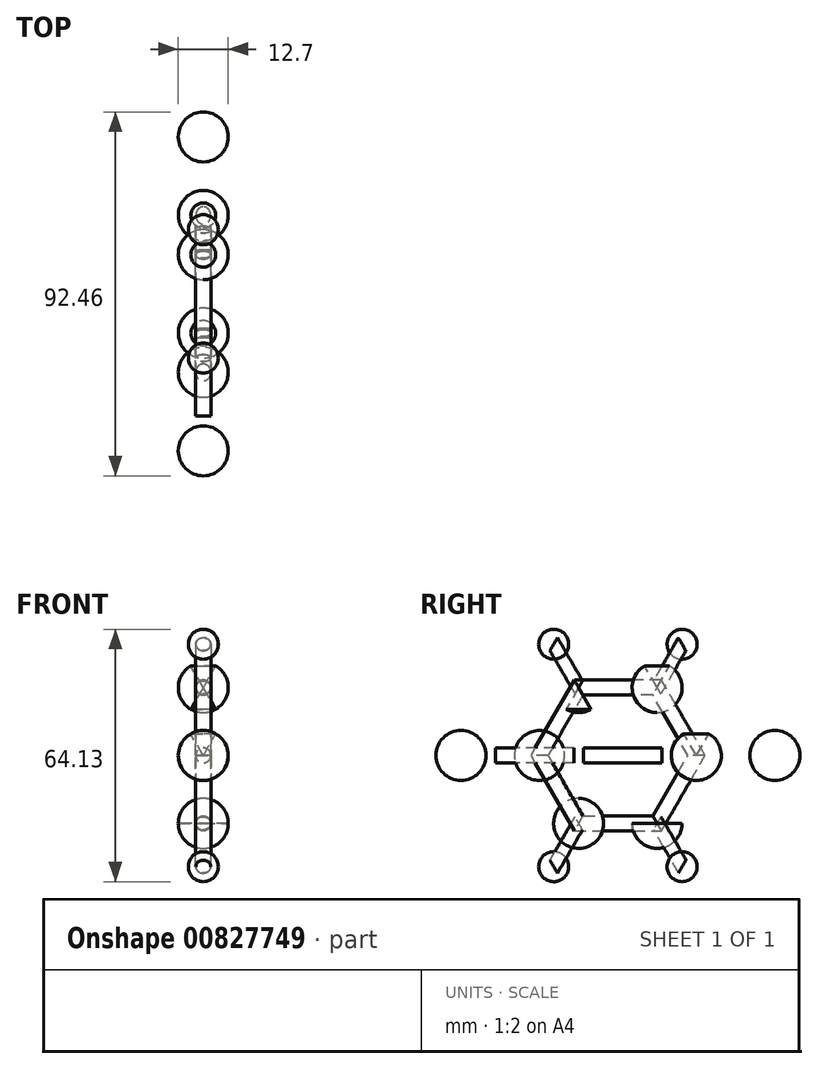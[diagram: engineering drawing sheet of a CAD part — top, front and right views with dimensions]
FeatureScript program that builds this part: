
annotation { "Feature Type Name" : "Feature", "Feature Type Description" : "" }
export const myFeature = defineFeature(function(context is Context, id is Id, definition is map)
    precondition{}
    {
        {
            var Q0;
            Q0=qCreatedBy(makeId("Front.planeOp"),FACE);
            var sketch = newSketch(context, id + "F0", { "sketchPlane" : qUnion([Q0])});
            skArc(sketch, "E0", {"start": v(0, 6.35) * mm, "mid": v(-6.35, 0) * mm, "end": v(0, -6.35) * mm});
            skLineSegment(sketch, "E1", {"start": v(0, 6.35) * mm, "end": v(0, -6.35) * mm});
            skSolve(sketch);
        }
        {
            var Q0;
            Q0=makeQuery(id+"F0.imprint","IMPRINT",FACE,{"disambiguationData":[TD([[makeQuery(id+"F0.imprint","IMPRINT",EDGE,{"derivedFrom":sQuery(id+"F0.wireOp",EDGE,"E0")}),1.0]])]});
            var Q1;
            Q1=sQuery(id+"F0.wireOp",EDGE,"E1");
            revolve(context, id + "F1", {"surfaceOperationType" : NewSurfaceOperationType.NEW, "entities" : qUnion([Q0]), "axis" : qUnion([Q1]), "revolveType" : RevolveType.FULL});
        }
        {
            var Q0;
            Q0=qCreatedBy(makeId("Right.planeOp"),FACE);
            var sketch = newSketch(context, id + "F2", { "sketchPlane" : qUnion([Q0])});
            skLineSegment(sketch, "E2", {"start": v(0, 0) * mm, "end": v(19.93, 0) * mm});
            skLineSegment(sketch, "E3", {"start": v(19.93, 0) * mm, "end": v(29.9, 17.26) * mm});
            skLineSegment(sketch, "E4", {"start": v(29.9, 17.26) * mm, "end": v(19.93, 34.52) * mm});
            skLineSegment(sketch, "E5", {"start": v(19.93, 34.52) * mm, "end": v(0, 34.52) * mm});
            skLineSegment(sketch, "E6", {"start": v(0, 34.52) * mm, "end": v(-9.96, 17.26) * mm});
            skLineSegment(sketch, "E7", {"start": v(-9.96, 17.26) * mm, "end": v(0, 0) * mm});
            skArc(sketch, "E8", {"start": v(19.93, 6.35) * mm, "mid": v(13.58, 0) * mm, "end": v(19.93, -6.35) * mm});
            skArc(sketch, "E9", {"start": v(29.9, 23.6) * mm, "mid": v(23.54, 17.26) * mm, "end": v(29.9, 10.9) * mm});
            skArc(sketch, "E10", {"start": v(19.93, 28.17) * mm, "mid": v(26.28, 34.52) * mm, "end": v(19.93, 40.87) * mm});
            skArc(sketch, "E11", {"start": v(-9.96, 23.6) * mm, "mid": v(-16.31, 17.26) * mm, "end": v(-9.96, 10.9) * mm});
            skLineSegment(sketch, "E12", {"start": v(19.93, 0) * mm, "end": v(19.93, 6.35) * mm});
            skLineSegment(sketch, "E13", {"start": v(19.93, 6.35) * mm, "end": v(19.93, -6.35) * mm});
            skLineSegment(sketch, "E14", {"start": v(29.9, 17.26) * mm, "end": v(29.9, 23.6) * mm});
            skLineSegment(sketch, "E15", {"start": v(29.9, 23.6) * mm, "end": v(29.9, 10.9) * mm});
            skLineSegment(sketch, "E16", {"start": v(19.93, 34.52) * mm, "end": v(19.93, 40.87) * mm});
            skLineSegment(sketch, "E17", {"start": v(19.93, 40.87) * mm, "end": v(19.93, 28.17) * mm});
            skLineSegment(sketch, "E18", {"start": v(0, 34.52) * mm, "end": v(0, 40.87) * mm});
            skLineSegment(sketch, "E19", {"start": v(0, 40.87) * mm, "end": v(0, 28.17) * mm});
            skLineSegment(sketch, "E20", {"start": v(-9.96, 17.26) * mm, "end": v(-9.96, 23.6) * mm});
            skLineSegment(sketch, "E21", {"start": v(-9.96, 23.6) * mm, "end": v(-9.96, 10.9) * mm});
            skArc(sketch, "E22.trimOffspring", {"start": v(0, 40.87) * mm, "mid": v(-6.13, 36.16) * mm, "end": v(-3.18, 29.02) * mm});
            skArc(sketch, "E23", {"start": v(0, 40.87) * mm, "mid": v(-6.35, 34.52) * mm, "end": v(0, 28.17) * mm});
            skLineSegment(sketch, "E24", {"start": v(19.93, 34.52) * mm, "end": v(26.28, 45.51) * mm});
            skLineSegment(sketch, "E25", {"start": v(0, 34.52) * mm, "end": v(-6.35, 45.51) * mm});
            skLineSegment(sketch, "E26", {"start": v(19.93, 0) * mm, "end": v(26.28, -11) * mm});
            skLineSegment(sketch, "E27", {"start": v(0, 0) * mm, "end": v(-6.35, -11) * mm});
            skArc(sketch, "E28", {"start": v(26.28, 41.7) * mm, "mid": v(30.09, 45.51) * mm, "end": v(26.28, 49.32) * mm});
            skArc(sketch, "E29", {"start": v(-6.35, 49.32) * mm, "mid": v(-10.16, 45.51) * mm, "end": v(-6.35, 41.7) * mm});
            skArc(sketch, "E30", {"start": v(26.28, -7.19) * mm, "mid": v(22.47, -11) * mm, "end": v(26.28, -14.8) * mm});
            skArc(sketch, "E31", {"start": v(-6.35, -14.8) * mm, "mid": v(-2.54, -11) * mm, "end": v(-6.35, -7.19) * mm});
            skLineSegment(sketch, "E32", {"start": v(26.28, 45.51) * mm, "end": v(26.28, 49.32) * mm});
            skLineSegment(sketch, "E33", {"start": v(26.28, 49.32) * mm, "end": v(26.28, 41.7) * mm});
            skLineSegment(sketch, "E34", {"start": v(-6.35, 45.51) * mm, "end": v(-6.35, 49.32) * mm});
            skLineSegment(sketch, "E35", {"start": v(-6.35, 49.32) * mm, "end": v(-6.35, 41.7) * mm});
            skLineSegment(sketch, "E36", {"start": v(-6.35, -11) * mm, "end": v(-6.35, -7.19) * mm});
            skLineSegment(sketch, "E37", {"start": v(-6.35, -7.19) * mm, "end": v(-6.35, -14.8) * mm});
            skLineSegment(sketch, "E38", {"start": v(26.28, -11) * mm, "end": v(26.28, -7.19) * mm});
            skLineSegment(sketch, "E39", {"start": v(26.28, -7.19) * mm, "end": v(26.28, -14.8) * mm});
            skSolve(sketch);
        }
        {
            var Q0;
            {var subQ0=sQuery(id+"F2.wireOp",EDGE,"E19");var subQ3=sQuery(id+"F2.wireOp",EDGE,"E23");var subQ5=makeQuery(id+"F2.imprint","INTERSECT",VERTEX,{"disambiguationData":[OD(0.0)],"derivedFrom":[subQ0,subQ3]});Q0=makeQuery(id+"F2.imprint","IMPRINT",FACE,{"disambiguationData":[TD([[makeQuery(id+"F2.imprint","IMPRINT",EDGE,{"disambiguationData":[TD([[subQ5,-1.0]])],"derivedFrom":subQ3}),1.0]])]});}
            var Q1;
            {var subQ0=sQuery(id+"F2.wireOp",EDGE,"E19");var subQ3=sQuery(id+"F2.wireOp",EDGE,"E23");var subQ5=makeQuery(id+"F2.imprint","INTERSECT",VERTEX,{"disambiguationData":[OD(1.0)],"derivedFrom":[subQ0,subQ3]});Q1=makeQuery(id+"F2.imprint","IMPRINT",FACE,{"disambiguationData":[TD([[makeQuery(id+"F2.imprint","IMPRINT",EDGE,{"disambiguationData":[TD([[subQ5,1.0]])],"derivedFrom":subQ3}),1.0]])]});}
            var Q2;
            {var subQ0=sQuery(id+"F2.wireOp",EDGE,"E25");var subQ3=sQuery(id+"F2.wireOp",EDGE,"E23");var subQ5=makeQuery(id+"F2.imprint","INTERSECT",VERTEX,{"derivedFrom":[subQ3,subQ0]});Q2=makeQuery(id+"F2.imprint","IMPRINT",FACE,{"disambiguationData":[TD([[makeQuery(id+"F2.imprint","IMPRINT",EDGE,{"disambiguationData":[TD([[subQ5,-1.0]])],"derivedFrom":subQ3}),1.0]])]});}
            var Q3;
            Q3=sQuery(id+"F2.wireOp",EDGE,"E18");
            revolve(context, id + "F3", {"surfaceOperationType" : NewSurfaceOperationType.NEW, "entities" : qUnion([Q0, Q1, Q2]), "axis" : qUnion([Q3]), "revolveType" : RevolveType.FULL});
        }
        {
            var Q0;
            {var subQ0=sQuery(id+"F2.wireOp",EDGE,"E11");Q0=makeQuery(id+"F2.imprint","IMPRINT",FACE,{"disambiguationData":[TD([[makeQuery(id+"F2.imprint","IMPRINT",EDGE,{"derivedFrom":subQ0}),1.0]])]});}
            var Q1;
            Q1=sQuery(id+"F2.wireOp",EDGE,"E20");
            revolve(context, id + "F4", {"surfaceOperationType" : NewSurfaceOperationType.NEW, "entities" : qUnion([Q0]), "axis" : qUnion([Q1]), "revolveType" : RevolveType.FULL});
        }
        {
            var Q0;
            {var subQ0=sQuery(id+"F2.wireOp",EDGE,"E24");var subQ3=sQuery(id+"F2.wireOp",EDGE,"E10");var subQ5=makeQuery(id+"F2.imprint","INTERSECT",VERTEX,{"derivedFrom":[subQ3,subQ0]});Q0=makeQuery(id+"F2.imprint","IMPRINT",FACE,{"disambiguationData":[TD([[makeQuery(id+"F2.imprint","IMPRINT",EDGE,{"disambiguationData":[TD([[subQ5,1.0]])],"derivedFrom":subQ3}),1.0]])]});}
            var Q1;
            {var subQ0=sQuery(id+"F2.wireOp",EDGE,"E17");var subQ3=sQuery(id+"F2.wireOp",EDGE,"E10");var subQ5=makeQuery(id+"F2.imprint","INTERSECT",VERTEX,{"disambiguationData":[OD(0.0)],"derivedFrom":[subQ3,subQ0]});Q1=makeQuery(id+"F2.imprint","IMPRINT",FACE,{"disambiguationData":[TD([[makeQuery(id+"F2.imprint","IMPRINT",EDGE,{"disambiguationData":[TD([[subQ5,-1.0]])],"derivedFrom":subQ3}),1.0]])]});}
            var Q2;
            {var subQ0=sQuery(id+"F2.wireOp",EDGE,"E17");var subQ1=sQuery(id+"F2.wireOp",EDGE,"E10");var subQ2=makeQuery(id+"F2.imprint","INTERSECT",VERTEX,{"disambiguationData":[OD(1.0)],"derivedFrom":[subQ1,subQ0]});Q2=makeQuery(id+"F2.imprint","IMPRINT",FACE,{"disambiguationData":[TD([[makeQuery(id+"F2.imprint","IMPRINT",EDGE,{"disambiguationData":[TD([[subQ2,1.0]])],"derivedFrom":subQ1}),1.0]])]});}
            var Q3;
            Q3=sQuery(id+"F2.wireOp",EDGE,"E17");
            revolve(context, id + "F5", {"surfaceOperationType" : NewSurfaceOperationType.NEW, "entities" : qUnion([Q0, Q1, Q2]), "axis" : qUnion([Q3]), "revolveType" : RevolveType.FULL});
        }
        {
            var Q0;
            {var subQ0=sQuery(id+"F2.wireOp",EDGE,"E15");var subQ3=sQuery(id+"F2.wireOp",EDGE,"E9");var subQ5=makeQuery(id+"F2.imprint","INTERSECT",VERTEX,{"disambiguationData":[OD(0.0)],"derivedFrom":[subQ3,subQ0]});Q0=makeQuery(id+"F2.imprint","IMPRINT",FACE,{"disambiguationData":[TD([[makeQuery(id+"F2.imprint","IMPRINT",EDGE,{"disambiguationData":[TD([[subQ5,-1.0]])],"derivedFrom":subQ3}),1.0]])]});}
            var Q1;
            {var subQ0=sQuery(id+"F2.wireOp",EDGE,"E15");var subQ3=sQuery(id+"F2.wireOp",EDGE,"E9");var subQ5=makeQuery(id+"F2.imprint","INTERSECT",VERTEX,{"disambiguationData":[OD(1.0)],"derivedFrom":[subQ3,subQ0]});Q1=makeQuery(id+"F2.imprint","IMPRINT",FACE,{"disambiguationData":[TD([[makeQuery(id+"F2.imprint","IMPRINT",EDGE,{"disambiguationData":[TD([[subQ5,1.0]])],"derivedFrom":subQ3}),1.0]])]});}
            var Q2;
            {var subQ1=sQuery(id+"F2.wireOp",EDGE,"E3");var subQ3=sQuery(id+"F2.wireOp",EDGE,"E9");var subQ4=makeQuery(id+"F2.imprint","INTERSECT",VERTEX,{"derivedFrom":[subQ1,subQ3]});Q2=makeQuery(id+"F2.imprint","IMPRINT",FACE,{"disambiguationData":[TD([[makeQuery(id+"F2.imprint","IMPRINT",EDGE,{"disambiguationData":[TD([[subQ4,1.0]])],"derivedFrom":subQ3}),1.0]])]});}
            var Q3;
            Q3=sQuery(id+"F2.wireOp",EDGE,"E14");
            revolve(context, id + "F6", {"surfaceOperationType" : NewSurfaceOperationType.NEW, "entities" : qUnion([Q0, Q1, Q2]), "axis" : qUnion([Q3]), "revolveType" : RevolveType.FULL});
        }
        {
            var Q0;
            {var subQ0=sQuery(id+"F2.wireOp",EDGE,"E13");var subQ3=sQuery(id+"F2.wireOp",EDGE,"E8");var subQ5=makeQuery(id+"F2.imprint","INTERSECT",VERTEX,{"disambiguationData":[OD(0.0)],"derivedFrom":[subQ3,subQ0]});Q0=makeQuery(id+"F2.imprint","IMPRINT",FACE,{"disambiguationData":[TD([[makeQuery(id+"F2.imprint","IMPRINT",EDGE,{"disambiguationData":[TD([[subQ5,-1.0]])],"derivedFrom":subQ3}),1.0]])]});}
            var Q1;
            {var subQ0=sQuery(id+"F2.wireOp",EDGE,"E13");var subQ3=sQuery(id+"F2.wireOp",EDGE,"E8");var subQ5=makeQuery(id+"F2.imprint","INTERSECT",VERTEX,{"disambiguationData":[OD(1.0)],"derivedFrom":[subQ3,subQ0]});Q1=makeQuery(id+"F2.imprint","IMPRINT",FACE,{"disambiguationData":[TD([[makeQuery(id+"F2.imprint","IMPRINT",EDGE,{"disambiguationData":[TD([[subQ5,1.0]])],"derivedFrom":subQ3}),1.0]])]});}
            var Q2;
            Q2=sQuery(id+"F2.wireOp",EDGE,"E13");
            revolve(context, id + "F7", {"surfaceOperationType" : NewSurfaceOperationType.NEW, "entities" : qUnion([Q0, Q1]), "axis" : qUnion([Q2]), "revolveType" : RevolveType.FULL});
        }
        {
            var Q0;
            Q0=qCreatedBy(makeId("Front.planeOp"),FACE);
            var sketch = newSketch(context, id + "F8", { "sketchPlane" : qUnion([Q0])});
            skCircle(sketch, "E40", {"center": v(0, 0) * mm, "radius": 1.9 * mm});
            skSolve(sketch);
        }
        {
            var Q0;
            Q0=makeQuery(id+"F8.imprint","IMPRINT",FACE,{"disambiguationData":[TD([[makeQuery(id+"F8.imprint","IMPRINT",EDGE,{"derivedFrom":sQuery(id+"F8.wireOp",EDGE,"E40")}),1.0]])]});
            var Q1;
            Q1=sQuery(id+"F2.wireOp",EDGE,"E2");
            var Q2;
            Q2=sQuery(id+"F2.wireOp",EDGE,"E3");
            var Q3;
            Q3=sQuery(id+"F2.wireOp",EDGE,"E4");
            var Q4;
            Q4=sQuery(id+"F2.wireOp",EDGE,"E5");
            var Q5;
            Q5=sQuery(id+"F2.wireOp",EDGE,"E6");
            var Q6;
            Q6=sQuery(id+"F2.wireOp",EDGE,"E7");
            var Q7;
            Q7 = qConstructionFilter(qBodyType(qCreatedBy(id + "F10" ,EDGE), BodyType.WIRE), ConstructionObject.NO);
            sweep(context, id + "F9", {"profiles" : qUnion([Q0]), "path" : qUnion([Q1, Q2, Q3, Q4, Q5, Q6, Q7])});
        }
        {
            var Q0;
            Q0=qCreatedBy(makeId("Right.planeOp"),FACE);
            var sketch = newSketch(context, id + "F10", { "sketchPlane" : qUnion([Q0])});
            skLineSegment(sketch, "E41", {"start": v(0, 0) * mm, "end": v(-9.97, 17.27) * mm});
            skLineSegment(sketch, "E42", {"start": v(-9.97, 17.27) * mm, "end": v(-29.9, 17.27) * mm});
            skLineSegment(sketch, "E43", {"start": v(0, 0) * mm, "end": v(19.94, 0) * mm});
            skLineSegment(sketch, "E44", {"start": v(19.94, 0) * mm, "end": v(29.9, 17.27) * mm});
            skLineSegment(sketch, "E45", {"start": v(29.9, 17.27) * mm, "end": v(49.85, 17.27) * mm});
            skArc(sketch, "E46", {"start": v(49.85, 10.92) * mm, "mid": v(56.2, 17.27) * mm, "end": v(49.85, 23.62) * mm});
            skArc(sketch, "E47", {"start": v(-29.9, 23.62) * mm, "mid": v(-36.26, 17.27) * mm, "end": v(-29.9, 10.92) * mm});
            skLineSegment(sketch, "E48", {"start": v(-29.9, 17.27) * mm, "end": v(-29.9, 23.62) * mm});
            skLineSegment(sketch, "E49", {"start": v(-29.9, 23.62) * mm, "end": v(-29.9, 10.92) * mm});
            skLineSegment(sketch, "E50", {"start": v(49.85, 17.27) * mm, "end": v(49.85, 23.62) * mm});
            skLineSegment(sketch, "E51", {"start": v(49.85, 23.62) * mm, "end": v(49.85, 10.92) * mm});
            skSolve(sketch);
        }
        {
            var Q0;
            {var subQ0=sQuery(id+"F10.wireOp",EDGE,"E47");Q0=makeQuery(id+"F10.imprint","IMPRINT",FACE,{"disambiguationData":[TD([[makeQuery(id+"F10.imprint","IMPRINT",EDGE,{"derivedFrom":subQ0}),1.0]])]});}
            var Q1;
            Q1=sQuery(id+"F10.wireOp",EDGE,"E48");
            revolve(context, id + "F11", {"surfaceOperationType" : NewSurfaceOperationType.NEW, "entities" : qUnion([Q0]), "axis" : qUnion([Q1]), "revolveType" : RevolveType.FULL});
        }
        {
            var Q0;
            {var subQ0=sQuery(id+"F10.wireOp",EDGE,"E46");Q0=makeQuery(id+"F10.imprint","IMPRINT",FACE,{"disambiguationData":[TD([[makeQuery(id+"F10.imprint","IMPRINT",EDGE,{"derivedFrom":subQ0}),1.0]])]});}
            var Q1;
            Q1=sQuery(id+"F10.wireOp",EDGE,"E51");
            revolve(context, id + "F12", {"surfaceOperationType" : NewSurfaceOperationType.NEW, "entities" : qUnion([Q0]), "axis" : qUnion([Q1]), "revolveType" : RevolveType.FULL});
        }
        {
            var Q0;
            Q0=qCreatedBy(makeId("Front.planeOp"),FACE);
            cPlane(context, id + "F13", {"entities" : qUnion([Q0]), "cplaneType" : CPlaneType.OFFSET, "offset" : (.785 + (.785 * cos(60 * degree))) * mm, "width" : 152.4 * mm, "height" : 152.4 * mm});
        }
        {
            var Q0;
            Q0=qCreatedBy(id+"F13.planeOp",FACE);
            var sketch = newSketch(context, id + "F14", { "sketchPlane" : qUnion([Q0])});
            skLineSegment(sketch, "E52", {"start": v(0, 0) * mm, "end": v(0, 17.27) * mm});
            skCircle(sketch, "E53", {"center": v(0, 17.27) * mm, "radius": 1.9 * mm});
            skSolve(sketch);
        }
        {
            var Q0;
            Q0=makeQuery(id+"F14.imprint","IMPRINT",FACE,{"disambiguationData":[TD([[makeQuery(id+"F14.imprint","IMPRINT",EDGE,{"derivedFrom":sQuery(id+"F14.wireOp",EDGE,"E53")}),1.0]])]});
            var Q1;
            Q1=sQuery(id+"F10.wireOp",EDGE,"E42");
            sweep(context, id + "F15", {"profiles" : qUnion([Q0]), "path" : qUnion([Q1])});
        }
        {
            var Q0;
            Q0=qCreatedBy(makeId("Front.planeOp"),FACE);
            cPlane(context, id + "F16", {"entities" : qUnion([Q0]), "cplaneType" : CPlaneType.OFFSET, "offset" : (.785 + (.785 * cos(60 * degree))) * mm, "oppositeDirection" : true, "width" : 152.4 * mm, "height" : 152.4 * mm});
        }
        {
            var Q0;
            Q0=qCreatedBy(id+"F16.planeOp",FACE);
            var sketch = newSketch(context, id + "F17", { "sketchPlane" : qUnion([Q0])});
            skLineSegment(sketch, "E54", {"start": v(0, 0) * mm, "end": v(0, 17.27) * mm});
            skCircle(sketch, "E55", {"center": v(0, 17.27) * mm, "radius": 1.9 * mm});
            skSolve(sketch);
        }
        {
            var Q0;
            Q0=makeQuery(id+"F17.imprint","IMPRINT",FACE,{"disambiguationData":[TD([[makeQuery(id+"F17.imprint","IMPRINT",EDGE,{"derivedFrom":sQuery(id+"F17.wireOp",EDGE,"E55")}),1.0]])]});
            var Q1;
            Q1=sQuery(id+"F10.wireOp",EDGE,"E45");
            sweep(context, id + "F18", {"profiles" : qUnion([Q0]), "path" : qUnion([Q1])});
        }
        {
            var Q0;
            {var subQ0=sQuery(id+"F2.wireOp",EDGE,"E29");Q0=makeQuery(id+"F2.imprint","IMPRINT",FACE,{"disambiguationData":[TD([[makeQuery(id+"F2.imprint","IMPRINT",EDGE,{"derivedFrom":subQ0}),1.0]])]});}
            var Q1;
            Q1=sQuery(id+"F2.wireOp",EDGE,"E34");
            revolve(context, id + "F19", {"surfaceOperationType" : NewSurfaceOperationType.NEW, "entities" : qUnion([Q0]), "axis" : qUnion([Q1]), "revolveType" : RevolveType.FULL});
        }
        {
            var Q0;
            {var subQ0=sQuery(id+"F2.wireOp",EDGE,"E28");Q0=makeQuery(id+"F2.imprint","IMPRINT",FACE,{"disambiguationData":[TD([[makeQuery(id+"F2.imprint","IMPRINT",EDGE,{"derivedFrom":subQ0}),1.0]])]});}
            var Q1;
            Q1=sQuery(id+"F2.wireOp",EDGE,"E33");
            revolve(context, id + "F20", {"surfaceOperationType" : NewSurfaceOperationType.NEW, "entities" : qUnion([Q0]), "axis" : qUnion([Q1]), "revolveType" : RevolveType.FULL});
        }
        {
            var Q0;
            {var subQ0=sQuery(id+"F2.wireOp",EDGE,"E37");var subQ1=sQuery(id+"F2.wireOp",EDGE,"E27");var subQ2=makeQuery(id+"F2.imprint","INTERSECT",VERTEX,{"derivedFrom":[subQ1,subQ0]});Q0=makeQuery(id+"F2.imprint","IMPRINT",FACE,{"disambiguationData":[TD([[makeQuery(id+"F2.imprint","IMPRINT",EDGE,{"disambiguationData":[TD([[subQ2,1.0]])],"derivedFrom":subQ1}),1.0]])]});}
            var Q1;
            {var subQ0=sQuery(id+"F2.wireOp",EDGE,"E37");var subQ1=sQuery(id+"F2.wireOp",EDGE,"E27");var subQ2=makeQuery(id+"F2.imprint","INTERSECT",VERTEX,{"derivedFrom":[subQ1,subQ0]});Q1=makeQuery(id+"F2.imprint","IMPRINT",FACE,{"disambiguationData":[TD([[makeQuery(id+"F2.imprint","IMPRINT",EDGE,{"disambiguationData":[TD([[subQ2,1.0]])],"derivedFrom":subQ1}),-1.0]])]});}
            var Q2;
            Q2=sQuery(id+"F2.wireOp",EDGE,"E37");
            revolve(context, id + "F21", {"surfaceOperationType" : NewSurfaceOperationType.NEW, "entities" : qUnion([Q0, Q1]), "axis" : qUnion([Q2]), "revolveType" : RevolveType.FULL});
        }
        {
            var Q0;
            {var subQ0=sQuery(id+"F2.wireOp",EDGE,"E39");var subQ1=sQuery(id+"F2.wireOp",EDGE,"E26");var subQ2=makeQuery(id+"F2.imprint","INTERSECT",VERTEX,{"derivedFrom":[subQ1,subQ0]});Q0=makeQuery(id+"F2.imprint","IMPRINT",FACE,{"disambiguationData":[TD([[makeQuery(id+"F2.imprint","IMPRINT",EDGE,{"disambiguationData":[TD([[subQ2,1.0]])],"derivedFrom":subQ1}),-1.0]])]});}
            var Q1;
            {var subQ0=sQuery(id+"F2.wireOp",EDGE,"E39");var subQ1=sQuery(id+"F2.wireOp",EDGE,"E26");var subQ2=makeQuery(id+"F2.imprint","INTERSECT",VERTEX,{"derivedFrom":[subQ1,subQ0]});Q1=makeQuery(id+"F2.imprint","IMPRINT",FACE,{"disambiguationData":[TD([[makeQuery(id+"F2.imprint","IMPRINT",EDGE,{"disambiguationData":[TD([[subQ2,1.0]])],"derivedFrom":subQ1}),1.0]])]});}
            var Q2;
            Q2=sQuery(id+"F2.wireOp",EDGE,"E38");
            revolve(context, id + "F22", {"surfaceOperationType" : NewSurfaceOperationType.NEW, "entities" : qUnion([Q0, Q1]), "axis" : qUnion([Q2]), "revolveType" : RevolveType.FULL});
        }
        {
            var Q0;
            Q0=qCreatedBy(makeId("Top.planeOp"),FACE);
            var Q1;
            Q1=sQuery(id+"F2.wireOp",EDGE,"E4");
            cPlane(context, id + "F23", {"entities" : qUnion([Q0, Q1]), "cplaneType" : CPlaneType.LINE_ANGLE, "offset" : 25.4 * mm, "angle" : 0 * degree, "width" : 152.4 * mm, "height" : 152.4 * mm});
        }
        {
            var Q0;
            Q0=qCreatedBy(id+"F23.planeOp",FACE);
            var sketch = newSketch(context, id + "F24", { "sketchPlane" : qUnion([Q0])});
            skLineSegment(sketch, "E56", {"start": v(0, 9.97) * mm, "end": v(0, 19.94) * mm});
            skCircle(sketch, "E57", {"center": v(0, 19.94) * mm, "radius": 1.9 * mm});
            skSolve(sketch);
        }
        {
            var Q0;
            Q0 = qSketchRegion(id + "F24", true);
            var Q1;
            Q1=sQuery(id+"F2.wireOp",EDGE,"E24");
            sweep(context, id + "F25", {"profiles" : qUnion([Q0]), "path" : qUnion([Q1])});
        }
        {
            var Q0;
            Q0=qCreatedBy(makeId("Top.planeOp"),FACE);
            var Q1;
            Q1=sQuery(id+"F2.wireOp",EDGE,"E6");
            cPlane(context, id + "F26", {"entities" : qUnion([Q0, Q1]), "cplaneType" : CPlaneType.LINE_ANGLE, "offset" : 25.4 * mm, "angle" : 0 * degree, "width" : 152.4 * mm, "height" : 152.4 * mm});
        }
        {
            var Q0;
            Q0=qCreatedBy(id+"F26.planeOp",FACE);
            var sketch = newSketch(context, id + "F27", { "sketchPlane" : qUnion([Q0])});
            skCircle(sketch, "E58", {"center": v(0, 29.92) * mm, "radius": 1.9 * mm});
            skSolve(sketch);
        }
        {
            var Q0;
            Q0 = qSketchRegion(id + "F27", true);
            var Q1;
            Q1=sQuery(id+"F2.wireOp",EDGE,"E25");
            sweep(context, id + "F28", {"profiles" : qUnion([Q0]), "path" : qUnion([Q1])});
        }
        {
            var Q0;
            Q0=qCreatedBy(makeId("Top.planeOp"),FACE);
            var Q1;
            Q1=sQuery(id+"F10.wireOp",EDGE,"E44");
            cPlane(context, id + "F29", {"entities" : qUnion([Q0, Q1]), "cplaneType" : CPlaneType.LINE_ANGLE, "offset" : 25.4 * mm, "angle" : 0 * degree, "width" : 152.4 * mm, "height" : 152.4 * mm});
        }
        {
            var Q0;
            Q0=qCreatedBy(id+"F29.planeOp",FACE);
            var sketch = newSketch(context, id + "F30", { "sketchPlane" : qUnion([Q0])});
            skCircle(sketch, "E59", {"center": v(0, 10.02) * mm, "radius": 1.9 * mm});
            skSolve(sketch);
        }
        {
            var Q0;
            Q0 = qSketchRegion(id + "F30", true);
            var Q1;
            Q1=sQuery(id+"F2.wireOp",EDGE,"E26");
            sweep(context, id + "F31", {"profiles" : qUnion([Q0]), "path" : qUnion([Q1])});
        }
        {
            var Q0;
            Q0=sQuery(id+"F10.wireOp",EDGE,"E41");
            var Q1;
            Q1=qCreatedBy(makeId("Top.planeOp"),FACE);
            cPlane(context, id + "F32", {"entities" : qUnion([Q0, Q1]), "cplaneType" : CPlaneType.LINE_ANGLE, "offset" : 25.4 * mm, "angle" : 0 * degree, "width" : 152.4 * mm, "height" : 152.4 * mm});
        }
        {
            var Q0;
            Q0=qCreatedBy(id+"F32.planeOp",FACE);
            var sketch = newSketch(context, id + "F33", { "sketchPlane" : qUnion([Q0])});
            skCircle(sketch, "E60", {"center": v(0, 0) * mm, "radius": 1.9 * mm});
            skSolve(sketch);
        }
        {
            var Q0;
            Q0 = qSketchRegion(id + "F33", true);
            var Q1;
            Q1=sQuery(id+"F2.wireOp",EDGE,"E27");
            sweep(context, id + "F34", {"profiles" : qUnion([Q0]), "path" : qUnion([Q1])});
        }
    });
